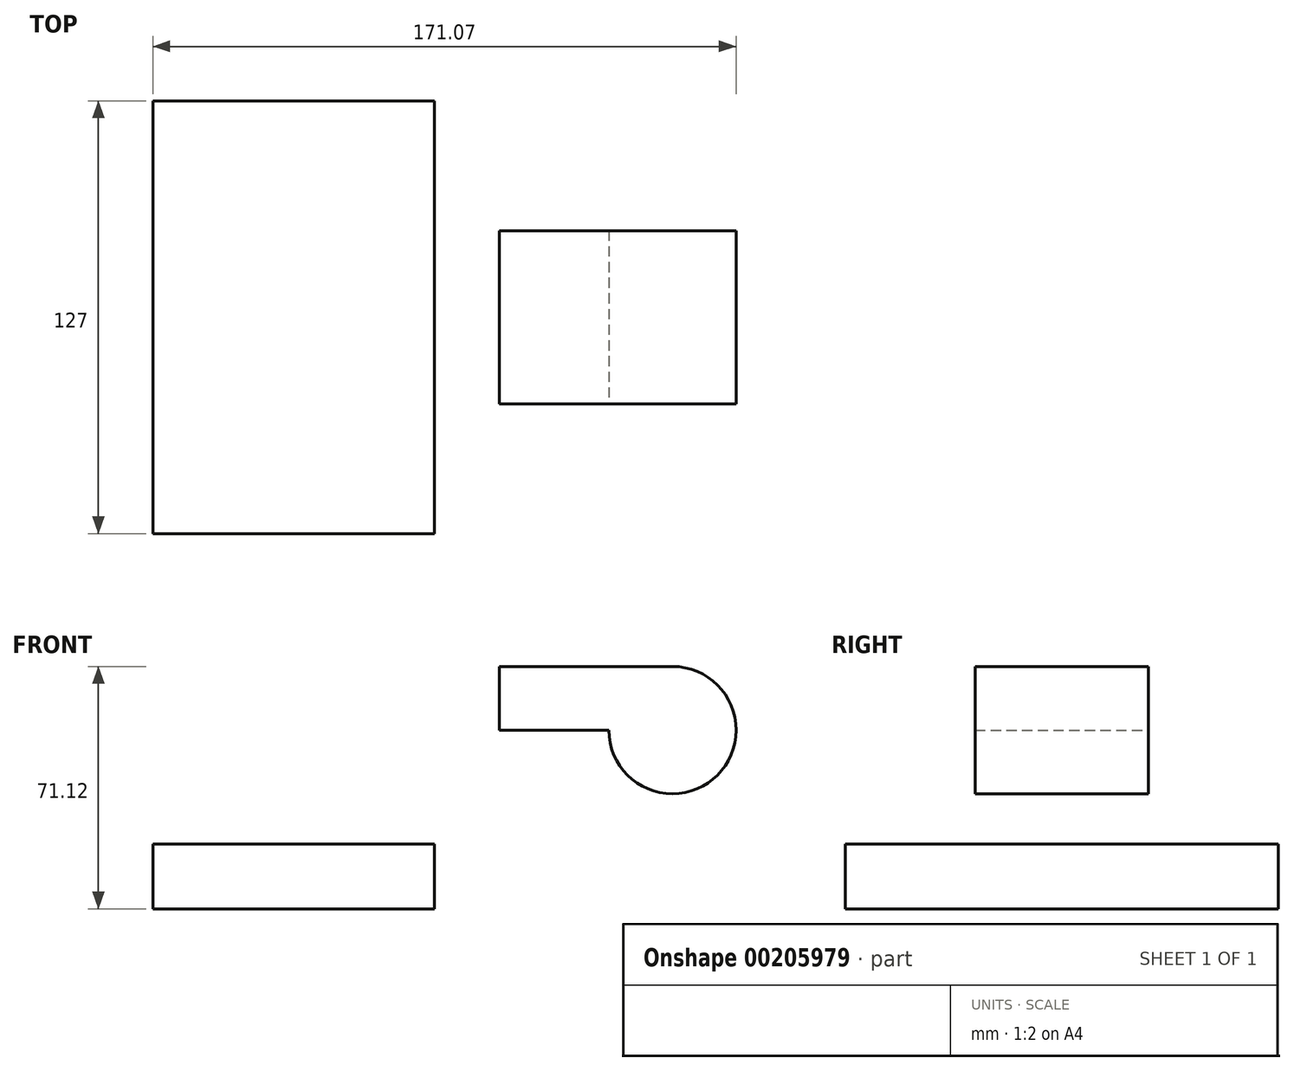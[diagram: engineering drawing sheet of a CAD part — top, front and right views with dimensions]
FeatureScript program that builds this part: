
annotation { "Feature Type Name" : "Feature", "Feature Type Description" : "" }
export const myFeature = defineFeature(function(context is Context, id is Id, definition is map)
    precondition{}
    {
        {
            var Q0;
            Q0=qCreatedBy(makeId("Front.planeOp"),FACE);
            var sketch = newSketch(context, id + "F0", { "sketchPlane" : qUnion([Q0])});
            skLineSegment(sketch, "E0.bottom", {"start": v(-41.28, 3.94) * mm, "end": v(41.27, 3.94) * mm});
            skLineSegment(sketch, "E0.top", {"start": v(-41.28, -15.11) * mm, "end": v(41.28, -15.11) * mm});
            skLineSegment(sketch, "E0.left", {"start": v(-41.28, 3.94) * mm, "end": v(-41.28, -15.11) * mm});
            skLineSegment(sketch, "E0.right", {"start": v(41.28, 3.94) * mm, "end": v(41.28, -15.11) * mm});
            skPoint(sketch, "E0.middle", {"position": v(0, -5.59) * mm});
            skLineSegment(sketch, "E1.bottom", {"start": v(60.32, 37.34) * mm, "end": v(111.12, 37.34) * mm});
            skLineSegment(sketch, "E1.top", {"start": v(60.32, 56) * mm, "end": v(111.12, 56) * mm});
            skLineSegment(sketch, "E1.left", {"start": v(60.32, 37.34) * mm, "end": v(60.32, 56) * mm});
            skLineSegment(sketch, "E1.right", {"start": v(111.12, 37.34) * mm, "end": v(111.12, 56) * mm});
            skPoint(sketch, "E1.middle", {"position": v(85.72, 46.67) * mm});
            skLineSegment(sketch, "E2", {"start": v(41.28, 3.94) * mm, "end": v(41.28, 21.41) * mm});
            skArc(sketch, "E3", {"start": v(41.27, 21.41) * mm, "mid": v(45.92, 32.64) * mm, "end": v(57.15, 37.29) * mm});
            skLineSegment(sketch, "E4", {"start": v(57.15, 37.29) * mm, "end": v(86, 37.29) * mm});
            skLineSegment(sketch, "E5.0", {"start": v(57.15, 56.34) * mm, "end": v(85.74, 56.34) * mm});
            skArc(sketch, "E5.1", {"start": v(22.22, 21.41) * mm, "mid": v(32.45, 46.1) * mm, "end": v(57.15, 56.34) * mm});
            skLineSegment(sketch, "E5.2", {"start": v(22.23, 3.94) * mm, "end": v(22.23, 21.41) * mm});
            skFitSpline(sketch, "E6", {"points": [v(-41.28, 3.94) * mm, v(57.15, 56.34) * mm], "startDerivative": vector(22.8, 86.52) * mm, "endDerivative": vector(103.96, 10.25) * mm});
            skSolve(sketch);
        }
        {
            var Q0;
            Q0=makeQuery(id+"F0.imprint","IMPRINT",FACE,{"disambiguationData":[TD([[makeQuery(id+"F0.imprint","IMPRINT",EDGE,{"derivedFrom":sQuery(id+"F0.wireOp",EDGE,"E0.bottom")}),-1.0]])]});
            extrude(context, id + "F1", {"entities" : qUnion([Q0]), "endBound" : BoundingType.SYMMETRIC, "depth" : 127 * mm});
        }
        {
            var Q0;
            {var subQ1=sQuery(id+"F0.wireOp",EDGE,"E2");Q0=makeQuery(id+"F0.imprint","IMPRINT",FACE,{"disambiguationData":[TD([[makeQuery(id+"F0.imprint","IMPRINT",EDGE,{"derivedFrom":subQ1}),1.0]])]});}
            var Q1;
            {var subQ3=sQuery(id+"F0.wireOp",EDGE,"E1.bottom");Q1=makeQuery(id+"F0.imprint","IMPRINT",FACE,{"disambiguationData":[TD([[makeQuery(id+"F0.imprint","IMPRINT",EDGE,{"derivedFrom":subQ3}),1.0]])]});}
            extrude(context, id + "F2", {"entities" : qUnion([Q0, Q1]), "operationType" : NewBodyOperationType.ADD, "endBound" : BoundingType.SYMMETRIC, "depth" : 50.8 * mm});
        }
        {
            var Q0;
            Q0=makeQuery(id+"F2.opExtrude","SWEPT_FACE",FACE,{"disambiguationData":[OSD([sQuery(id+"F0.wireOp",EDGE,"E1.right")])]});
            var Q1;
            Q1=makeQuery(id+"F2.opExtrude","SWEPT_EDGE",EDGE,{"disambiguationData":[OSD([sQuery(id+"F0.wireOp",EDGE,"E1.bottom"),sQuery(id+"F0.wireOp",EDGE,"E1.right")])]});
            revolve(context, id + "F3", {"operationType" : NewBodyOperationType.ADD, "entities" : qUnion([Q0]), "axis" : qUnion([Q1]), "revolveType" : RevolveType.FULL});
        }
    });
